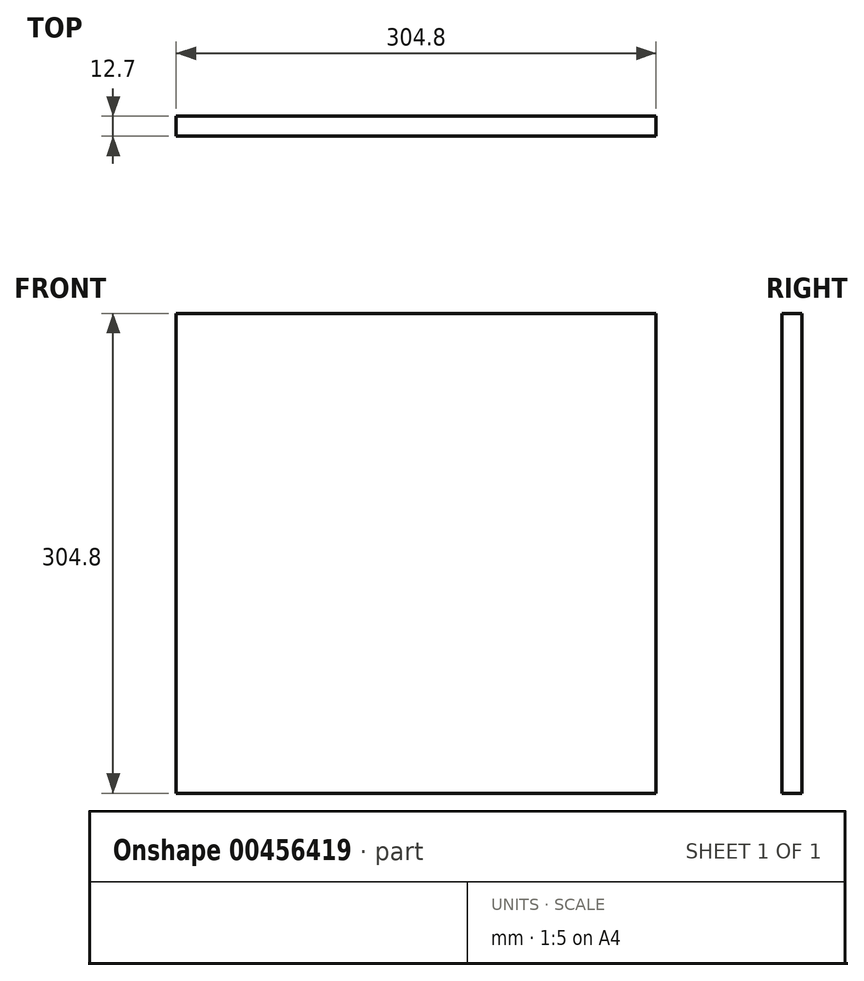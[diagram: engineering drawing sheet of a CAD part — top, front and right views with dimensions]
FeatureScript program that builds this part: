
annotation { "Feature Type Name" : "Feature", "Feature Type Description" : "" }
export const myFeature = defineFeature(function(context is Context, id is Id, definition is map)
    precondition{}
    {
        {
            var Q0;
            Q0=qCreatedBy(makeId("Front.planeOp"),FACE);
            var sketch = newSketch(context, id + "F0", { "sketchPlane" : qUnion([Q0])});
            skLineSegment(sketch, "E0.bottom", {"start": v(152.4, 152.4) * mm, "end": v(-152.4, 152.4) * mm});
            skLineSegment(sketch, "E0.top", {"start": v(152.4, -152.4) * mm, "end": v(-152.4, -152.4) * mm});
            skLineSegment(sketch, "E0.left", {"start": v(152.4, 152.4) * mm, "end": v(152.4, -152.4) * mm});
            skLineSegment(sketch, "E0.right", {"start": v(-152.4, 152.4) * mm, "end": v(-152.4, -152.4) * mm});
            skPoint(sketch, "E0.middle", {"position": v(0, 0) * mm});
            skSolve(sketch);
        }
        {
            var Q0;
            Q0 = qSketchRegion(id + "F0", true);
            extrude(context, id + "F1", {"entities" : qUnion([Q0]), "depth" : 12.7 * mm});
        }
    });
